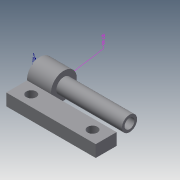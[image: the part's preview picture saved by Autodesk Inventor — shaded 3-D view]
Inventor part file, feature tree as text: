
AUTODESK INVENTOR PART (.ipt)
format: ipt  version: 2019 (Build 230136000, 136)  size: 267,776 bytes
history: native  units: mm
features: other x13, extrude x8, sketch x7, plane x5, direct_edit x3, projected_geometry x2, move_body x2, fillet x1
ambient origin geometry x8: Origin, YZ Plane, XZ Plane, XY Plane, X Axis, Y Axis, Z Axis, Center Point
bodies: Solid1 (feature_tree)
feature tree (41):
  other  "Annotations"
  extrude  "Extrusion1"  Depth=45.0mm
  sketch  "Sketch4"  dims[d5=5.0mm d6=5.0mm d7=11.0mm]
  extrude  "Extrusion4"  Depth=5.0mm
  fillet  "Fillet1"  Radius=11.0mm
  extrude  "Extrusion5"  Depth=23.0mm
  plane  "Work Plane1"
  extrude  "Extrusion6"  Depth=10.0mm
  plane  "Work Plane8"
  plane  "Work Plane10"
  sketch  "Sketch11"  dims[d24=3.0mm d25=0.0mm d26=12.0mm]
  plane  "Work Plane11"
  plane  "Work Plane12"
  extrude  "Extrusion10"  Depth=12.0mm
  extrude  "Extrusion11"  Depth=3.0mm TaperAngle=0.0deg
  direct_edit  "Direct Edit1"
  extrude  "Extrusion13"  Depth=6.5mm
  direct_edit  "Direct Edit2"
  sketch  "Sketch15"  dims[d33=5.0mm d34=5.0mm d35=18.0mm d36=7.0mm d37=18.0mm d38=7.1mm d39=30.8mm d40=7.1mm d41=3.0mm d42=0.0mm d52=0.0mm d53=0.0mm d54=0.0mm d55=10.0mm d56=0.0mm d57=10.0mm d58=0.0mm d59=0.0mm d60=0.0mm d61=-1.5mm d62=0.0mm d63=0.0mm d64=-17.25mm d68=1.6mm d69=10.0mm d70=0.0mm d77=-0.3mm d78=2.5mm d79=0.0mm d80=0.5mm d71=35.626875mm d72=6.5mm d75=48.705644mm d76=7.6mm]
  extrude  "Extrusion14"  Depth=18.0mm
  direct_edit  "Direct Edit3"
  sketch  "Sketch1"  dims[d0=6.0mm d1=0.0mm d4=45.0mm]
  sketch  "Sketch5"  dims[d8=11.0mm d9=23.0mm]
  sketch  "Sketch6"  dims[d10=10.0mm d20=13.0mm]
  projected_geometry  "Projected Loop4"
  sketch  "Sketch13"  dims[d27=5.0mm d28=3.0mm d29=0.0mm]
  projected_geometry  "Projected Loop5"
  other  "Composite2"
  move_body  "Move1"
  move_body  "Move2"
  other  "Size1"
  other  "Srf2"
  other  "Size2"
  other  "Radial Dimension 1"
  other  "Diameter Dimension 1"
  parser-record x2  (decoder bookkeeping rows leaked as tree rows — omitted from the tree; the rows remain in map.json)
  other  "Cerniera Assemb.iam"
  other  "Cerniera 1:2"
  other  "Cerniera_definitiva.iam"
  other  "Cerniera_cov:1"
note: 2 file-system paths scrubbed to <path> (originals preserved in map.json)
